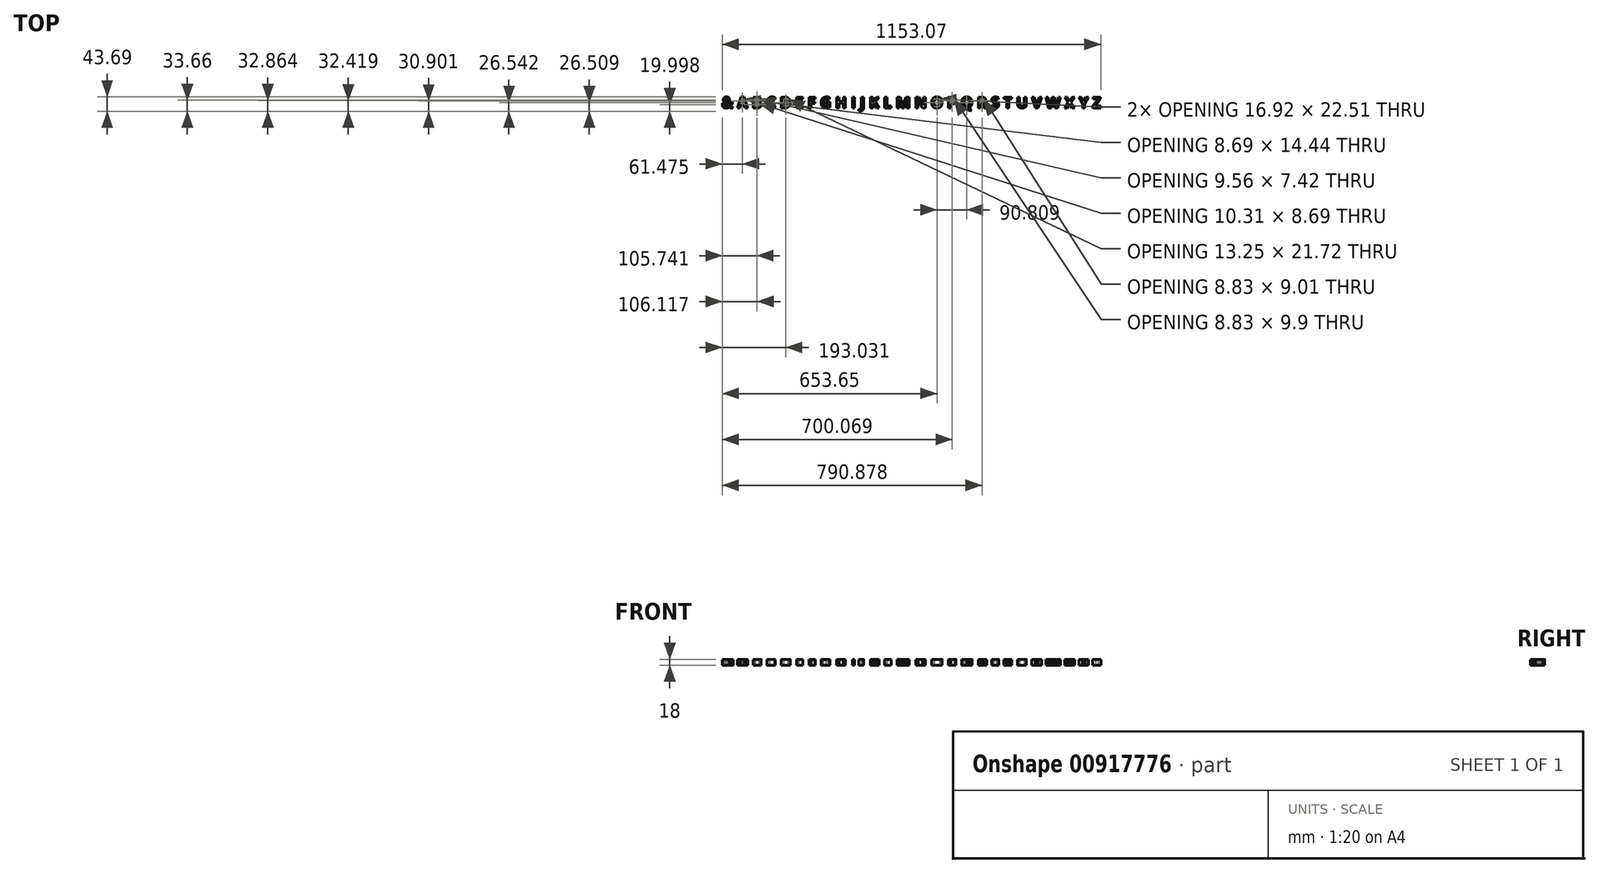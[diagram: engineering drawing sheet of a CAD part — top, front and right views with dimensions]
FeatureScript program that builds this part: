
annotation { "Feature Type Name" : "Feature", "Feature Type Description" : "" }
export const myFeature = defineFeature(function(context is Context, id is Id, definition is map)
    precondition{}
    {
        {
            var Q0;
            Q0=qCreatedBy(makeId("Top.planeOp"),FACE);
            var sketch = newSketch(context, id + "F0", { "sketchPlane" : qUnion([Q0])});
            skText(sketch, "E0", { "text": "& A B C D E F G H I J K L M N O P Q R S T U V W X Y Z", "fontName": "OpenSans-Bold.ttf"});
            const initialGuessF0  = {"E0": [-0.0533, -0.01518, 1, 0, 0.03364]};
            skSetInitialGuess(sketch, initialGuessF0);
            skSolve(sketch);
        }
        {
            var Q0;
            Q0 = qSketchRegion(id + "F0", true);
            extrude(context, id + "F1", {"entities" : qUnion([Q0]), "depth" : 18 * mm, "offsetDistance" : 25 * mm});
        }
        {
            var Q0;
            Q0=makeQuery(id+"F1.opExtrude","CAP_FACE",FACE,{"disambiguationData":[OSD([sQuery(id+"F0.wireOp",EDGE,"E0.sketch_text.stroke-0"),sQuery(id+"F0.wireOp",EDGE,"E0.sketch_text.stroke-1"),sQuery(id+"F0.wireOp",EDGE,"E0.sketch_text.stroke-2"),sQuery(id+"F0.wireOp",EDGE,"E0.sketch_text.stroke-3"),sQuery(id+"F0.wireOp",EDGE,"E0.sketch_text.stroke-4"),sQuery(id+"F0.wireOp",EDGE,"E0.sketch_text.stroke-5"),sQuery(id+"F0.wireOp",EDGE,"E0.sketch_text.stroke-6"),sQuery(id+"F0.wireOp",EDGE,"E0.sketch_text.stroke-7"),sQuery(id+"F0.wireOp",EDGE,"E0.sketch_text.stroke-8"),sQuery(id+"F0.wireOp",EDGE,"E0.sketch_text.stroke-9"),sQuery(id+"F0.wireOp",EDGE,"E0.sketch_text.stroke-10"),sQuery(id+"F0.wireOp",EDGE,"E0.sketch_text.stroke-11"),sQuery(id+"F0.wireOp",EDGE,"E0.sketch_text.stroke-12"),sQuery(id+"F0.wireOp",EDGE,"E0.sketch_text.stroke-13"),sQuery(id+"F0.wireOp",EDGE,"E0.sketch_text.stroke-14"),sQuery(id+"F0.wireOp",EDGE,"E0.sketch_text.stroke-15"),sQuery(id+"F0.wireOp",EDGE,"E0.sketch_text.stroke-16"),sQuery(id+"F0.wireOp",EDGE,"E0.sketch_text.stroke-17"),sQuery(id+"F0.wireOp",EDGE,"E0.sketch_text.stroke-18"),sQuery(id+"F0.wireOp",EDGE,"E0.sketch_text.stroke-19"),sQuery(id+"F0.wireOp",EDGE,"E0.sketch_text.stroke-20"),sQuery(id+"F0.wireOp",EDGE,"E0.sketch_text.stroke-21"),sQuery(id+"F0.wireOp",EDGE,"E0.sketch_text.stroke-22"),sQuery(id+"F0.wireOp",EDGE,"E0.sketch_text.stroke-23"),sQuery(id+"F0.wireOp",EDGE,"E0.sketch_text.stroke-24"),sQuery(id+"F0.wireOp",EDGE,"E0.sketch_text.stroke-25"),sQuery(id+"F0.wireOp",EDGE,"E0.sketch_text.stroke-26"),sQuery(id+"F0.wireOp",EDGE,"E0.sketch_text.stroke-27"),sQuery(id+"F0.wireOp",EDGE,"E0.sketch_text.stroke-28"),sQuery(id+"F0.wireOp",EDGE,"E0.sketch_text.stroke-29"),sQuery(id+"F0.wireOp",EDGE,"E0.sketch_text.stroke-30"),sQuery(id+"F0.wireOp",EDGE,"E0.sketch_text.stroke-31"),sQuery(id+"F0.wireOp",EDGE,"E0.sketch_text.stroke-32"),sQuery(id+"F0.wireOp",EDGE,"E0.sketch_text.stroke-33")])],"isStart":true});
            fillet(context, id + "F2", {"entities" : qUnion([Q0]), "radius" : 0.8 * mm, "tangentPropagation" : true, "allowEdgeOverflow" : false});
        }
    });
